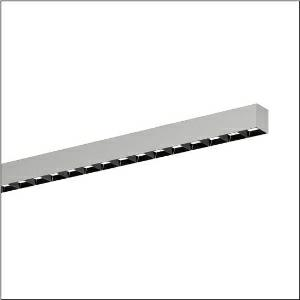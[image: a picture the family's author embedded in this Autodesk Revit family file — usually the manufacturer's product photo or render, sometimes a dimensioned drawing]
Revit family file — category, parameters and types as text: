
# Revit family: silica_r__21_51mx21dc4asb_ccd6
name_source: partatom
category: Lighting Fixtures
units: mm (PartAtom-declared; Revit-internal decimal feet)

## family parameters
Cut with Voids When Loaded = No
Host = Face
Light Source = No
Part Type = Normal
Room Calculation Point = No
Round Connector Dimension = Use Diameter
Shared = No

## types (1)
- --- (1 x LED, 10800 lm, 64.8 W, 4000K)
    Apparent Load = 65 VA
    CIE Flux Codes = 87 99 100 100 100
    Color Rendering = 80
    Color Temperature = 4000K
    Default Elevation = 1800 mm
    Description = Silica® 21, office luminaire, primary light control with darklight reflector, of PMMA, black, CAT 2 (L<= 3000cd/m²), light emission: direct distribution, primary light characteristic: symmetric, installation type: surface-mounted, LED, rated luminous flux: 10.800lm, luminous efficacy: 167lm/W, light colour: 840, colour temperature: 4000K, control gear: DALI 2, with terminal, 3+2-pole, max. 2.5mm², mains connection: 220..240V, AC, 50/60Hz, rated input power: 64.8W, luminaire housing, of aluminium, metallic grey (RAL 9006), length: 3.004mm, width: 53mm, height: 53mm, protection rating (complete): IP20, insulation class (complete): insulation class I (protective earthing), certification: CE, permissible operating ambient temperature: 0..+35°C, standard: EN 50419, packaging unit: 1 piece
    Height = 53 mm
    Lamp = 1 x LED
    Lamp Light Flux = 10800 lm
    Lamp Power = 64.8 W
    Lamp count = 1
    Length = 3004 mm
    Luminous efficacy = 167 lm/W
    Manufacturer = Siteco
    ModVariant = No
    Model = 51MX21DC4ASB
    Mounting Place = Ceiling
    Mounting Type = Surface mounted
    Number of Poles = 1
    OnlyDefault = Yes
    Power Factor = 1
    Product Name = Silica® 21
    Product group = office luminaire | ceiling mounted
    ProductGroupID = 302
    Protection Class = Protection class I
    Protection Degree = IP 20
    RLX_Detail_Level = 1
    RLX_Emergency_Light_Flux = 0 lm
    RLX_Emergency_Type = 0
    RLX_Emergency_Type_DB = No
    RlxData = <blob elided: 63125 chars, md5=9c6dcf30>
    Socket = socket
    Standby Power = 0 W
    System Light Flux = 10800 lm
    System Power = 65 W
    Type Comments = factory setting: luminous flux: 100 % | dim-lin: 254 | 367 mA
    Type Image = l_1335929.jpg
    URL = http://relux.com
    VarID = @adj_123538
    Voltage = 0 V
    Weight = 0.00 kg
    Width = 53 mm

## geometry (parser evidence)
native form markers: Blend x4, Sweep x11
no freeform markers — native parametric forms only
